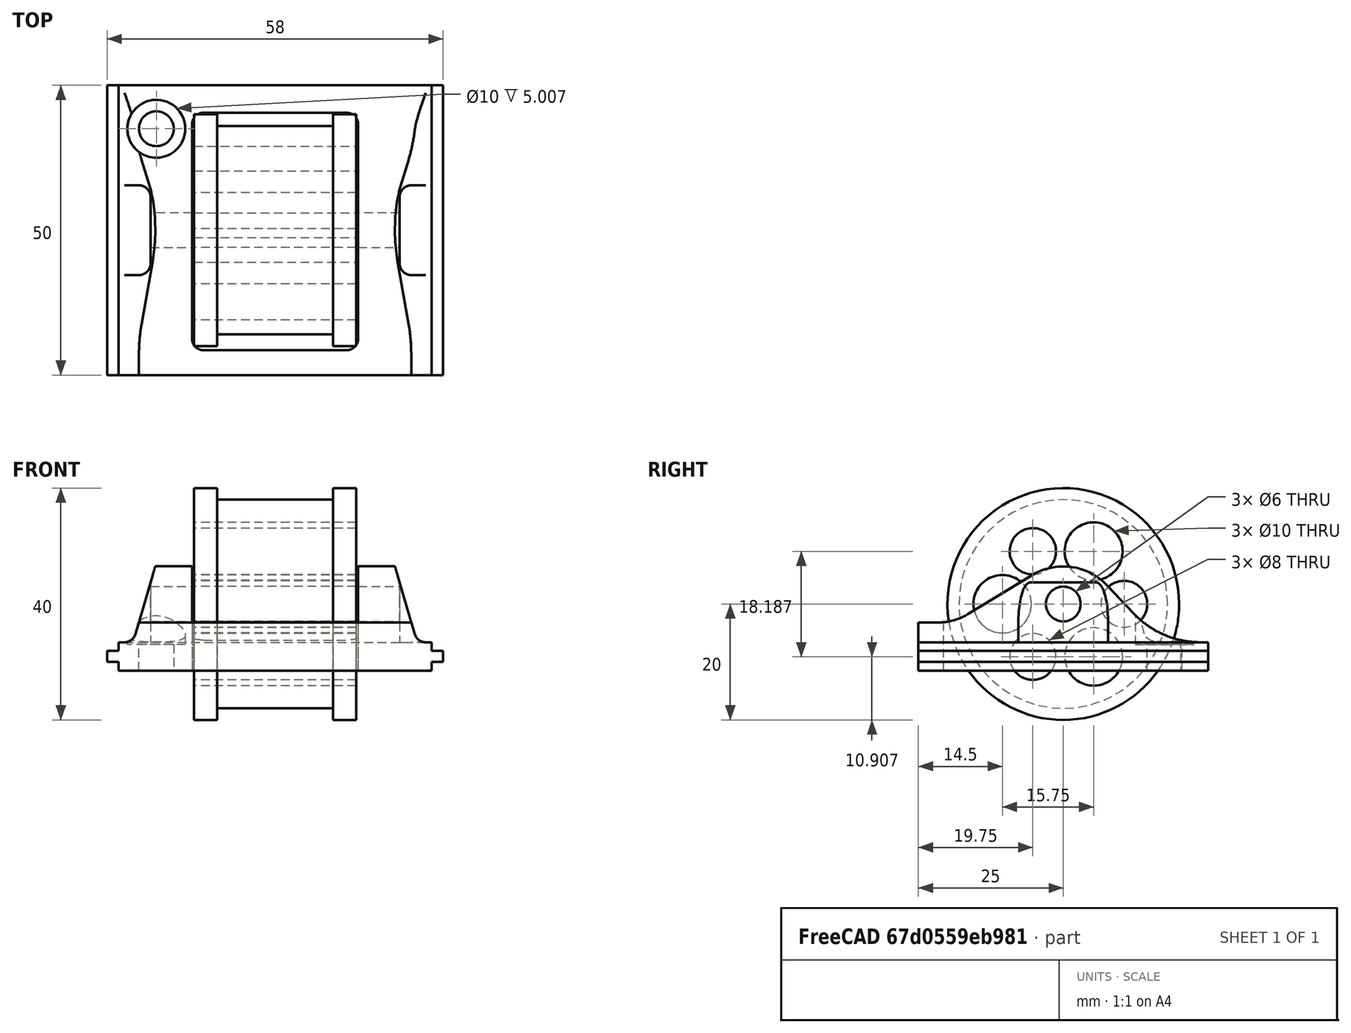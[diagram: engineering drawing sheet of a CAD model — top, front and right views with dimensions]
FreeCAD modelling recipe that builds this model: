
FCSTD DOCUMENT  (FreeCAD 0.22R35966 (Git))
Label: pusher
License: All rights reserved
LicenseURL: http://en.wikipedia.org/wiki/All_rights_reserved
objects: Sketcher::SketchObject×9, TechDraw::DrawViewDimension×9, PartDesign::Pocket×6, TechDraw::DrawProjGroupItem×3, PartDesign::Pad×2, PartDesign::Plane×2, PartDesign::Body×2, App::Part×2, Spreadsheet::Sheet×1, TechDraw::DrawProjGroup×1, TechDraw::DrawViewPart×1, TechDraw::DrawViewAnnotation×1, TechDraw::DrawViewSection×1, TechDraw::DrawViewSymbol×1, TechDraw::DrawSVGTemplate×1, TechDraw::DrawPage×1
note: 29 computed .brp shape members not serialized (recipe doc carries the construction recipe); baked Part::Feature solids carry a one-line shape summary decoded from their .brp

FEATURE [Spreadsheet::Sheet] Spreadsheet  label="dim"
  cells = A2='Rail Height; B2(railHeight)=2; A3='Spring OD; B3(springOD)=40; A4='Rail from floor; B4(railFromFloor)=10; A5='Spring ID; B5(springID)=36; A6='spring Width; B6(springWidth)=20; A7='cylinder Width; B7(cylinderWidth)==springWidth + 8; A8='Rail Width; B8(railWidth)=58; A9='Rail top; B9(railTop)=1.5; A10='Axis OD; B10(axisOD)=6; A11='pilar Width; B11(pilarWidth)=6; A12='Rail Depth; B12(RailDepth)=2; A13='RBF OD; B13(RBFOD)=6; A14='RBF Seating D; B14(RBFSeatingD)=10; A15='RBF From Sat; B15(RBFFromSat)=7.5; A16='RBF From Rail; B16(RBFFromRail)=6.5
FEATURE [Sketcher::SketchObject] Sketch001
  FullyConstrained = false
  MapMode = 5
  Placement = pos=(0,0,0) rot=(0.57735,0.57735,0.57735;2.0944rad)
  Support = -> [YZ_Plane]
  expr: Constraints[10] = Sketch.Constraints[10]
  expr: Constraints[11] = Sketch.Constraints[11]
  expr: Constraints[12] = Sketch.Constraints[12]
  expr: Constraints[13] = Sketch.Constraints[13]
  expr: Constraints[16] = Sketch.Constraints[16]
  expr: Constraints[9] = Sketch.Constraints[9]
  sketch-geometry (21):
    g0: LineSegment StartX=-43.3303 StartY=12 StartZ=0 EndX=0 EndY=12 EndZ=0
    g1: LineSegment StartX=0 StartY=12 StartZ=0 EndX=0 EndY=10 EndZ=0
    g2: LineSegment StartX=0 StartY=10 StartZ=0 EndX=-43.3303 EndY=10 EndZ=0
    g3: LineSegment StartX=-43.3303 StartY=10 StartZ=0 EndX=-43.3303 EndY=12 EndZ=0
    g4: Circle CenterX=-25 CenterY=20 CenterZ=0 NormalX=0 NormalY=0 NormalZ=1 AngleXU=0 Radius=20
    g5: Circle CenterX=-25 CenterY=20 CenterZ=0 NormalX=0 NormalY=0 NormalZ=1 AngleXU=0 Radius=18
    g6: Circle CenterX=-25 CenterY=20 CenterZ=0 NormalX=0 NormalY=0 NormalZ=1 AngleXU=0 Radius=20
    g7: Circle CenterX=-25 CenterY=20 CenterZ=0 NormalX=0 NormalY=0 NormalZ=1 AngleXU=0 Radius=3
    g8: LineSegment StartX=-19.75 StartY=29.0933 StartZ=0 EndX=-30.25 EndY=29.0933 EndZ=0
    g9: LineSegment StartX=-30.25 StartY=29.0933 StartZ=0 EndX=-35.5 EndY=20 EndZ=0
    g10: LineSegment StartX=-35.5 StartY=20 StartZ=0 EndX=-30.25 EndY=10.9067 EndZ=0
    g11: LineSegment StartX=-30.25 StartY=10.9067 StartZ=0 EndX=-19.75 EndY=10.9067 EndZ=0
    g12: LineSegment StartX=-19.75 StartY=10.9067 StartZ=0 EndX=-14.5 EndY=20 EndZ=0
    g13: LineSegment StartX=-14.5 StartY=20 StartZ=0 EndX=-19.75 EndY=29.0933 EndZ=0
    g14: Circle CenterX=-25 CenterY=20 CenterZ=0 NormalX=0 NormalY=0 NormalZ=1 AngleXU=0 Radius=10.5
    g15: Circle CenterX=-19.75 CenterY=29.0933 CenterZ=0 NormalX=0 NormalY=0 NormalZ=1 AngleXU=0 Radius=5
    g16: Circle CenterX=-14.5 CenterY=20 CenterZ=0 NormalX=0 NormalY=0 NormalZ=1 AngleXU=0 Radius=4
    g17: Circle CenterX=-19.75 CenterY=10.9067 CenterZ=0 NormalX=0 NormalY=0 NormalZ=1 AngleXU=0 Radius=5
    g18: Circle CenterX=-30.25 CenterY=10.9067 CenterZ=0 NormalX=0 NormalY=0 NormalZ=1 AngleXU=0 Radius=4
    g19: Circle CenterX=-35.5 CenterY=20 CenterZ=0 NormalX=0 NormalY=0 NormalZ=1 AngleXU=0 Radius=5
    g20: Circle CenterX=-30.25 CenterY=29.0933 CenterZ=0 NormalX=0 NormalY=0 NormalZ=1 AngleXU=0 Radius=4
  constraints (49):
    c: Coincident(g0,g1)
    c: Coincident(g1,g2)
    c: Coincident(g2,g3)
    c: Coincident(g3,g0)
    c: Horizontal(g0)
    c: Horizontal(g2)
    c: Vertical(g1)
    c: Vertical(g3)
    c: PointOnObject(g0,g-2)
    c: Diameter(g4) = 40
    c: DistanceY(g-1,g4) = 20
    c: DistanceX(g4,g-1) = 25
    c: DistanceY(g1,g1) = 2
    c: DistanceY(g-1,g1) = 10
    c: PointOnObject(g0,g4)
    c: Coincident(g5,g4)
    c: Diameter(g5) = 36
    c: Coincident(g6,g4)
    c: Equal(g6,g4)
    c: Coincident(g7,g6)
    c: Diameter(g7) = 6
    c: Coincident(g8,g9)
    c: Coincident(g9,g10)
    c: Coincident(g10,g11)
    c: Coincident(g11,g12)
    c: Coincident(g12,g13)
    c: Coincident(g13,g8)
    c: Equal(g8, g9-g13) x5
    c: PointOnObject(g8,g14)
    c: PointOnObject(g9,g14)
    c: PointOnObject(g10,g14)
    c: PointOnObject(g11,g14)
    c: PointOnObject(g12,g14)
    c: PointOnObject(g13,g14)
    c: Horizontal(g8)
    c: Coincident(g14,g6)
    c: Coincident(g15,g8)
    c: Coincident(g16,g12)
    c: Coincident(g17,g11)
    c: Coincident(g18,g10)
    c: Coincident(g19,g9)
    c: Coincident(g20,g8)
    c: Diameter(g20) = 8
    c: Equal(g20,g16)
    c: Equal(g20,g18)
    c: Diameter(g15) = 10
    c: Equal(g15,g17)
    c: Equal(g15,g19)
    c: Diameter(g14) = 21
FEATURE [PartDesign::Pad] Pad
  AllowMultiFace = false
  Direction = (1,1,1)
  Length = 28
  Length2 = 100
  Midplane = true
  Placement = pos=(0,0,0) rot=(0.57735,0.57735,0.57735;2.0944rad)
  Profile = -> Sketch001
  Suppressed = false
  Type = 0
  expr: Length = <<dim>>.cylinderWidth
FEATURE [Sketcher::SketchObject] Sketch002
  FullyConstrained = false
  MapMode = 5
  Placement = pos=(0,0,0) rot=(0.57735,0.57735,0.57735;2.0944rad)
  Support = -> [YZ_Plane]
  expr: Constraints[10] = Sketch.Constraints[10]
  expr: Constraints[11] = Sketch.Constraints[11]
  expr: Constraints[12] = Sketch.Constraints[12]
  expr: Constraints[13] = Sketch.Constraints[13]
  expr: Constraints[16] = Sketch.Constraints[16]
  expr: Constraints[9] = Sketch.Constraints[9]
  sketch-geometry (6):
    g0: LineSegment StartX=-43.3303 StartY=12 StartZ=0 EndX=0 EndY=12 EndZ=0
    g1: LineSegment StartX=0 StartY=12 StartZ=0 EndX=0 EndY=10 EndZ=0
    g2: LineSegment StartX=0 StartY=10 StartZ=0 EndX=-43.3303 EndY=10 EndZ=0
    g3: LineSegment StartX=-43.3303 StartY=10 StartZ=0 EndX=-43.3303 EndY=12 EndZ=0
    g4: Circle CenterX=-25 CenterY=20 CenterZ=0 NormalX=0 NormalY=0 NormalZ=1 AngleXU=0 Radius=20
    g5: Circle CenterX=-25 CenterY=20 CenterZ=0 NormalX=0 NormalY=0 NormalZ=1 AngleXU=0 Radius=18
  constraints (17):
    c: Coincident(g0,g1)
    c: Coincident(g1,g2)
    c: Coincident(g2,g3)
    c: Coincident(g3,g0)
    c: Horizontal(g0)
    c: Horizontal(g2)
    c: Vertical(g1)
    c: Vertical(g3)
    c: PointOnObject(g0,g-2)
    c: Diameter(g4) = 40
    c: DistanceY(g-1,g4) = 20
    c: DistanceX(g4,g-1) = 25
    c: DistanceY(g1,g1) = 2
    c: DistanceY(g-1,g1) = 10
    c: PointOnObject(g0,g4)
    c: Coincident(g5,g4)
    c: Diameter(g5) = 36
FEATURE [PartDesign::Pocket] Pocket
  AllowMultiFace = false
  BaseFeature = -> Pad
  Direction = (1,1,1)
  Length = 20
  Length2 = 100
  Midplane = true
  Placement = pos=(0,0,0) rot=(0.57735,0.57735,0.57735;2.0944rad)
  Profile = -> Sketch002
  Suppressed = false
  Type = 0
  expr: Length = <<dim>>.springWidth
FEATURE [Sketcher::SketchObject] Sketch003
  FullyConstrained = false
  MapMode = 5
  Placement = pos=(0,0,0) rot=(1,0,0;1.5708rad)
  Support = -> [XZ_Plane001]
  expr: Constraints[31] = <<dim>>.railFromFloor
  expr: Constraints[37] = <<dim>>.railHeight - 0.1
  expr: Constraints[44] = <<dim>>.railWidth
  expr: Constraints[45] = <<dim>>.RailDepth
  sketch-geometry (20):
    g0: LineSegment StartX=27 StartY=8.5 StartZ=0 EndX=27 EndY=10 EndZ=0
    g1: LineSegment StartX=27 StartY=10 StartZ=0 EndX=29 EndY=10 EndZ=0
    g2: LineSegment StartX=29 StartY=10 StartZ=0 EndX=29 EndY=11.9 EndZ=0
    g3: LineSegment StartX=29 StartY=11.9 StartZ=0 EndX=27 EndY=11.9 EndZ=0
    g4: LineSegment StartX=27 StartY=11.9 StartZ=0 EndX=27 EndY=13.4 EndZ=0
    g5: LineSegment StartX=27 StartY=13.4 StartZ=0 EndX=26 EndY=13.4 EndZ=0
    g6: LineSegment StartX=24.0797 StartY=14.8411 StartZ=0 EndX=20.25 EndY=28 EndZ=0
    g7: LineSegment StartX=20.25 StartY=28 StartZ=0 EndX=14.25 EndY=28 EndZ=0
    g8: LineSegment StartX=-27 StartY=8.5 StartZ=0 EndX=-27 EndY=10 EndZ=0
    g9: LineSegment StartX=-27 StartY=10 StartZ=0 EndX=-29 EndY=10 EndZ=0
    g10: LineSegment StartX=-29 StartY=10 StartZ=0 EndX=-29 EndY=11.9 EndZ=0
    g11: LineSegment StartX=-29 StartY=11.9 StartZ=0 EndX=-27 EndY=11.9 EndZ=0
    g12: LineSegment StartX=-27 StartY=11.9 StartZ=0 EndX=-27 EndY=13.4 EndZ=0
    g13: LineSegment StartX=-27 StartY=13.4 StartZ=0 EndX=-26 EndY=13.4 EndZ=0
    g14: LineSegment StartX=-24.0797 StartY=14.8411 StartZ=0 EndX=-20.25 EndY=28 EndZ=0
    g15: LineSegment StartX=-20.25 StartY=28 StartZ=0 EndX=-14.25 EndY=28 EndZ=0
    g16: LineSegment StartX=14.25 StartY=28 StartZ=0 EndX=-14.25 EndY=28 EndZ=0
    g17: LineSegment StartX=-27 StartY=8.5 StartZ=0 EndX=27 EndY=8.5 EndZ=0
    g18: ArcOfCircle CenterX=-26 CenterY=15.4 CenterZ=0 NormalX=0 NormalY=0 NormalZ=1 AngleXU=0 Radius=2 StartAngle=4.71239 EndAngle=5.99997
    g19: ArcOfCircle CenterX=26 CenterY=15.4 CenterZ=0 NormalX=0 NormalY=0 NormalZ=1 AngleXU=0 Radius=2 StartAngle=3.4248 EndAngle=4.71239
  constraints (57):
    c: Vertical(g0)
    c: Coincident(g0,g1)
    c: Horizontal(g1)
    c: Coincident(g1,g2)
    c: Vertical(g2)
    c: Coincident(g2,g3)
    c: Horizontal(g3)
    c: Coincident(g3,g4)
    c: Coincident(g4,g5)
    c: Horizontal(g5)
    c: Coincident(g6,g7)
    c: Horizontal(g7)
    c: Vertical(g4)
    c: PointOnObject(g3,g0)
    c: Vertical(g8)
    c: Coincident(g8,g9)
    c: Horizontal(g9)
    c: Coincident(g9,g10)
    c: Vertical(g10)
    c: Coincident(g10,g11)
    c: Horizontal(g11)
    c: Coincident(g11,g12)
    c: Coincident(g12,g13)
    c: Horizontal(g13)
    c: Coincident(g14,g15)
    c: Horizontal(g15)
    c: Vertical(g12)
    c: PointOnObject(g11,g8)
    c: Coincident(g17,g8)
    c: Coincident(g17,g0)
    c: Symmetric(g8,g0,g-2)
    c: DistanceY(g-1,g9) = 10
    c: Equal(g8,g0)
    c: Equal(g9,g1)
    c: Equal(g2,g10)
    c: Equal(g12,g4)
    c: Equal(g5,g13)
    c: DistanceY(g10,g10) = 1.9
    c: Equal(g8,g12)
    c: DistanceY(g12,g12) = 1.5
    c: Equal(g15,g7)
    c: DistanceX(g16,g16) = 28.5
    c: DistanceY(g-1,g15) = 28  'pilarHeight'
    c: DistanceX(g15,g15) = 6
    c: DistanceX(g9,g1) = 58
    c: DistanceX(g1,g1) = 2
    c: Tangent(g14,g18) = -1.5708
    c: Tangent(g13,g18) = -1.5708
    c: Tangent(g6,g19) = 1.5708
    c: Tangent(g5,g19) = 1.5708
    c: Equal(g18,g19)
    c: Equal(g13,g5)
    c: Radius(g18) = 2
    c: DistanceX(g12,g18) = 1
    c: Coincident(g16,g15)
    c: Coincident(g16,g7)
    c: Symmetric(g7,g15,g-2)
FEATURE [PartDesign::Pad] Pad001
  AllowMultiFace = false
  Direction = (1,1,1)
  Length = 50
  Length2 = 100
  Placement = pos=(0,0,0) rot=(1,0,0;1.5708rad)
  Profile = -> Sketch003
  Suppressed = false
  Type = 0
FEATURE [Sketcher::SketchObject] Sketch004  label="baseSketch001"
  FullyConstrained = false
  MapMode = 5
  Placement = pos=(0,0,0) rot=(0.57735,0.57735,0.57735;2.0944rad)
  Support = -> [YZ_Plane001]
  expr: Constraints[18] = <<dim>>.axisOD
  expr: Constraints[36] = 10 + 1.9 + 1.5
  expr: Constraints[9] = <<dim>>.springOD
  sketch-geometry (19):
    g0: LineSegment StartX=-43.3303 StartY=12 StartZ=0 EndX=0 EndY=12 EndZ=0
    g1: LineSegment StartX=0 StartY=12 StartZ=0 EndX=0 EndY=10 EndZ=0
    g2: LineSegment StartX=0 StartY=10 StartZ=0 EndX=-43.3303 EndY=10 EndZ=0
    g3: LineSegment StartX=-43.3303 StartY=10 StartZ=0 EndX=-43.3303 EndY=12 EndZ=0
    g4: Circle CenterX=-25 CenterY=20 CenterZ=0 NormalX=0 NormalY=0 NormalZ=1 AngleXU=0 Radius=20
    g5: Circle CenterX=-25 CenterY=20 CenterZ=0 NormalX=0 NormalY=0 NormalZ=1 AngleXU=0 Radius=18
    g6: Circle CenterX=-25 CenterY=20 CenterZ=0 NormalX=0 NormalY=0 NormalZ=1 AngleXU=0 Radius=3
    g7: LineSegment StartX=-41.4553 StartY=18.2442 StartZ=0 EndX=-30.3662 EndY=24.9932 EndZ=0
    g8: LineSegment StartX=-17.5118 StartY=23.2798 StartZ=0 EndX=-12.821 EndY=18.3352 EndZ=0
    g9: LineSegment StartX=-1.33651 StartY=13.4 StartZ=0 EndX=5.50918 EndY=13.4 EndZ=0
    g10: LineSegment StartX=5.50918 StartY=13.4 StartZ=0 EndX=5.50918 EndY=39.591 EndZ=0
    g11: LineSegment StartX=5.50918 StartY=39.591 StartZ=0 EndX=-54.9003 EndY=39.591 EndZ=0
    g12: LineSegment StartX=-54.9003 StartY=39.591 StartZ=0 EndX=-54.9003 EndY=16.8241 EndZ=0
    g13: LineSegment StartX=-25 StartY=47.8975 StartZ=0 EndX=-25 EndY=-22.7529 EndZ=0
    g14: ArcOfCircle CenterX=-1.33651 CenterY=29.2301 CenterZ=0 NormalX=0 NormalY=0 NormalZ=1 AngleXU=0 Radius=15.8301 StartAngle=3.90065 EndAngle=4.71239
    g15: ArcOfCircle CenterX=-25 CenterY=16.176 CenterZ=0 NormalX=0 NormalY=0 NormalZ=1 AngleXU=0 Radius=10.3217 StartAngle=0.759059 EndAngle=2.11752
    g16: GeomPoint X=-25 Y=26.4977 Z=0
    g17: LineSegment StartX=-54.9003 StartY=16.8241 StartZ=0 EndX=-46.5205 EndY=16.8241 EndZ=0
    g18: ArcOfCircle CenterX=-46.5205 CenterY=26.5668 CenterZ=0 NormalX=0 NormalY=0 NormalZ=1 AngleXU=0 Radius=9.74273 StartAngle=4.71239 EndAngle=5.25911
  constraints (43):
    c: Coincident(g0,g1)
    c: Coincident(g1,g2)
    c: Coincident(g2,g3)
    c: Coincident(g3,g0)
    c: Horizontal(g0)
    c: Horizontal(g2)
    c: Vertical(g1)
    c: Vertical(g3)
    c: PointOnObject(g0,g-2)
    c: Diameter(g4) = 40
    c: DistanceY(g-1,g4) = 20  'H'
    c: DistanceX(g4,g-1) = 25  'centerFromBack'
    c: DistanceY(g1,g1) = 2
    c: DistanceY(g-1,g1) = 10
    c: PointOnObject(g0,g4)
    c: Coincident(g5,g4)
    c: Diameter(g5) = 36
    c: Coincident(g6,g4)
    c: Diameter(g6) = 6
    c: Horizontal(g9)
    c: Coincident(g9,g10)
    c: Vertical(g10)
    c: Coincident(g10,g11)
    c: Horizontal(g11)
    c: Coincident(g11,g12)
    c: Vertical(g12)
    c: PointOnObject(g6,g13)
    c: Tangent(g8,g14) = -1.5708
    c: Tangent(g9,g14) = -1.5708
    c: PointOnObject(g15,g13)
    c: Coincident(g15,g7)
    c: Coincident(g15,g8)
    c: Tangent(g7,g15) = 1.5708
    c: Tangent(g8,g15) = 1.5708
    c: PointOnObject(g16,g15)
    c: PointOnObject(g16,g13)
    c: DistanceY(g-1,g9) = 13.4
    c: Vertical(g13)
    c: Coincident(g17,g12)
    c: Coincident(g18,g7)
    c: Tangent(g7,g18) = -1.5708
    c: Horizontal(g17)
    c: Tangent(g17,g18) = -1.5708
FEATURE [PartDesign::Pocket] Pocket001
  AllowMultiFace = false
  BaseFeature = -> Pad001
  Direction = (1,1,1)
  Length = 5
  Length2 = 100
  Midplane = true
  Placement = pos=(0,0,0) rot=(1,0,0;1.5708rad)
  Profile = -> Sketch004
  Suppressed = false
  Type = 1
FEATURE [PartDesign::Plane] DatumPlane
  AttachmentOffset = pos=(0,0,28) rot=(0,0,1;0rad)
  Length = 71.1909
  MapMode = 3
  Placement = pos=(0,0,28) rot=(0,0,1;3.14159rad)
  ResizeMode = 0
  Support = -> [Pocket001]
  Width = 88.1909
FEATURE [Sketcher::SketchObject] Sketch005
  FullyConstrained = false
  MapMode = 5
  Placement = pos=(0,0,28) rot=(0,0,1;3.14159rad)
  Support = -> [DatumPlane]
  expr: Constraints[31] = <<dim>>.railWidth
  expr: Constraints[6] = Sketch004.Constraints.centerFromBack
  sketch-geometry (13):
    g0: LineSegment StartX=-29 StartY=32.75 StartZ=0 EndX=-23.5 EndY=32.75 EndZ=0
    g1: LineSegment StartX=-21.5 StartY=30.75 StartZ=0 EndX=-21.5 EndY=19.25 EndZ=0
    g2: LineSegment StartX=-23.5 StartY=17.25 StartZ=0 EndX=-29 EndY=17.25 EndZ=0
    g3: LineSegment StartX=-29 StartY=17.25 StartZ=0 EndX=-29 EndY=32.75 EndZ=0
    g4: LineSegment StartX=-29 StartY=25 StartZ=0 EndX=29 EndY=25 EndZ=0
    g5: ArcOfCircle CenterX=-23.5 CenterY=30.75 CenterZ=0 NormalX=0 NormalY=0 NormalZ=1 AngleXU=0 Radius=2 StartAngle=5e-16 EndAngle=1.5708
    g6: ArcOfCircle CenterX=-23.5 CenterY=19.25 CenterZ=0 NormalX=0 NormalY=0 NormalZ=1 AngleXU=0 Radius=2 StartAngle=4.71239 EndAngle=6.28319
    g7: LineSegment StartX=29 StartY=32.75 StartZ=0 EndX=23.5 EndY=32.75 EndZ=0
    g8: LineSegment StartX=21.5 StartY=30.75 StartZ=0 EndX=21.5 EndY=19.25 EndZ=0
    g9: LineSegment StartX=23.5 StartY=17.25 StartZ=0 EndX=29 EndY=17.25 EndZ=0
    g10: LineSegment StartX=29 StartY=17.25 StartZ=0 EndX=29 EndY=32.75 EndZ=0
    g11: ArcOfCircle CenterX=23.5 CenterY=30.75 CenterZ=0 NormalX=0 NormalY=0 NormalZ=1 AngleXU=0 Radius=2 StartAngle=1.5708 EndAngle=3.14159
    g12: ArcOfCircle CenterX=23.5 CenterY=19.25 CenterZ=0 NormalX=0 NormalY=0 NormalZ=1 AngleXU=0 Radius=2 StartAngle=3.14159 EndAngle=4.71239
  constraints (32):
    c: Coincident(g2,g3)
    c: Coincident(g3,g0)
    c: Horizontal(g0)
    c: Horizontal(g2)
    c: Vertical(g3)
    c: Horizontal(g4)
    c: DistanceY(g-1,g4) = 25
    c: Tangent(g1,g5) = 1.5708
    c: Tangent(g0,g5) = 1.5708
    c: Tangent(g1,g6) = 1.5708
    c: Tangent(g2,g6) = 1.5708
    c: Equal(g6,g5)
    c: Radius(g5) = 2
    c: Symmetric(g1,g1,g4)
    c: DistanceY(g1,g1) = 11.5
    c: Coincident(g9,g10)
    c: Coincident(g10,g7)
    c: Horizontal(g7)
    c: Horizontal(g9)
    c: Vertical(g10)
    c: Tangent(g8,g11) = -1.5708
    c: Tangent(g7,g11) = -1.5708
    c: Tangent(g8,g12) = -1.5708
    c: Tangent(g9,g12) = -1.5708
    c: Equal(g12,g11)
    c: Symmetric(g8,g1,g-2)
    c: DistanceX(g1,g8) = 43
    c: Symmetric(g8,g8,g4)
    c: PointOnObject(g4,g3)
    c: PointOnObject(g4,g10)
    c: Symmetric(g9,g2,g-2)
    c: DistanceX(g0,g7) = 58
FEATURE [PartDesign::Pocket] Pocket002
  AllowMultiFace = false
  BaseFeature = -> Pocket001
  Direction = (1,1,1)
  Length = 14.6
  Length2 = 100
  Placement = pos=(0,0,0) rot=(1,0,0;1.5708rad)
  Profile = -> Sketch005
  Suppressed = false
  Type = 0
FEATURE [Sketcher::SketchObject] Sketch006
  FullyConstrained = false
  MapMode = 5
  Support = -> [XY_Plane001]
  sketch-geometry (8):
    g0: LineSegment StartX=-12.3486 StartY=-4.73756 StartZ=0 EndX=12.3447 EndY=-4.73756 EndZ=0
    g1: LineSegment StartX=14.3447 StartY=-6.73756 StartZ=0 EndX=14.3447 EndY=-43.7105 EndZ=0
    g2: LineSegment StartX=12.3447 StartY=-45.7105 StartZ=0 EndX=-12.3486 EndY=-45.7105 EndZ=0
    g3: LineSegment StartX=-14.3486 StartY=-43.7105 StartZ=0 EndX=-14.3486 EndY=-6.73756 EndZ=0
    g4: ArcOfCircle CenterX=12.3447 CenterY=-6.73756 CenterZ=0 NormalX=0 NormalY=0 NormalZ=1 AngleXU=0 Radius=2 StartAngle=1e-16 EndAngle=1.5708
    g5: ArcOfCircle CenterX=-12.3486 CenterY=-6.73756 CenterZ=0 NormalX=0 NormalY=0 NormalZ=1 AngleXU=0 Radius=2 StartAngle=1.5708 EndAngle=3.14159
    g6: ArcOfCircle CenterX=-12.3486 CenterY=-43.7105 CenterZ=0 NormalX=0 NormalY=0 NormalZ=1 AngleXU=0 Radius=2 StartAngle=3.14159 EndAngle=4.71239
    g7: ArcOfCircle CenterX=12.3447 CenterY=-43.7105 CenterZ=0 NormalX=0 NormalY=0 NormalZ=1 AngleXU=0 Radius=2 StartAngle=4.71239 EndAngle=6.28319
  constraints (16):
    c: Horizontal(g0)
    c: Horizontal(g2)
    c: Vertical(g1)
    c: Vertical(g3)
    c: Tangent(g1,g4) = 1.5708
    c: Tangent(g0,g4) = 1.5708
    c: Tangent(g0,g5) = 1.5708
    c: Tangent(g3,g5) = 1.5708
    c: Tangent(g3,g6) = 1.5708
    c: Tangent(g2,g6) = 1.5708
    c: Tangent(g1,g7) = 1.5708
    c: Tangent(g2,g7) = 1.5708
    c: Equal(g4,g5)
    c: Equal(g5,g6)
    c: Equal(g6,g7)
    c: Radius(g4) = 2
FEATURE [PartDesign::Pocket] Pocket003
  AllowMultiFace = false
  BaseFeature = -> Pocket002
  Direction = (1,1,1)
  Length = 5
  Length2 = 100
  Midplane = true
  Placement = pos=(0,0,0) rot=(1,0,0;1.5708rad)
  Profile = -> Sketch006
  Reversed = true
  Suppressed = false
  Type = 1
FEATURE [PartDesign::Plane] DatumPlane001
  AttachmentOffset = pos=(0,0,18) rot=(0,0,1;0rad)
  Length = 71.1909
  MapMode = 5
  Placement = pos=(0,0,18) rot=(0,0,1;0rad)
  ResizeMode = 0
  Support = -> [XY_Plane001]
  Width = 88.1909
FEATURE [Sketcher::SketchObject] Sketch007
  FullyConstrained = false
  MapMode = 5
  Placement = pos=(0,0,18) rot=(0,0,1;0rad)
  Support = -> [DatumPlane001]
  expr: Constraints[0] = <<dim>>.RBFSeatingD
  expr: Constraints[1] = <<dim>>.RBFFromSat
  expr: Constraints[2] = <<dim>>.railWidth / 2 - <<dim>>.RailDepth - <<dim>>.RBFFromRail
  sketch-geometry (1):
    g0: Circle CenterX=-20.5 CenterY=-7.5 CenterZ=0 NormalX=0 NormalY=0 NormalZ=1 AngleXU=0 Radius=5
  constraints (3):
    c: Diameter(g0) = 10
    c: DistanceY(g0,g-1) = 7.5
    c: DistanceX(g0,g-1) = 20.5
FEATURE [PartDesign::Pocket] Pocket004
  AllowMultiFace = false
  BaseFeature = -> Pocket003
  Direction = (1,1,1)
  Length = 10
  Length2 = 100
  Midplane = true
  Placement = pos=(0,0,0) rot=(1,0,0;1.5708rad)
  Profile = -> Sketch007
  Suppressed = false
  Type = 0
FEATURE [Sketcher::SketchObject] Sketch008
  FullyConstrained = false
  MapMode = 5
  Placement = pos=(0,0,18) rot=(0,0,1;0rad)
  Support = -> [DatumPlane001]
  expr: Constraints[0] = <<dim>>.RBFOD
  expr: Constraints[1] = <<dim>>.RBFFromSat
  expr: Constraints[2] = <<dim>>.railWidth / 2 - <<dim>>.RailDepth - <<dim>>.RBFFromRail
  sketch-geometry (1):
    g0: Circle CenterX=-20.5 CenterY=-7.5 CenterZ=0 NormalX=0 NormalY=0 NormalZ=1 AngleXU=0 Radius=3
  constraints (3):
    c: Diameter(g0) = 6
    c: DistanceY(g0,g-1) = 7.5
    c: DistanceX(g0,g-1) = 20.5
FEATURE [PartDesign::Pocket] Pocket005
  AllowMultiFace = false
  BaseFeature = -> Pocket004
  Direction = (1,1,1)
  Length = 5
  Length2 = 100
  Placement = pos=(0,0,0) rot=(1,0,0;1.5708rad)
  Profile = -> Sketch008
  Suppressed = false
  Type = 1
FEATURE [Sketcher::SketchObject] Sketch  label="baseSketch"
  FullyConstrained = true
  MapMode = 5
  Placement = pos=(-21.5,0,0) rot=(0.707107,0,-0.707107;3.14159rad)
  Support = -> [Pocket005]
  expr: Constraints[10] = <<dim>>.springOD / 2
  expr: Constraints[11] = <<dim>>.springOD / 2 + 5
  expr: Constraints[12] = <<dim>>.railHeight
  expr: Constraints[13] = <<dim>>.railFromFloor
  expr: Constraints[16] = <<dim>>.springID
  expr: Constraints[9] = <<dim>>.springOD
  sketch-geometry (6):
    g0: LineSegment StartX=-43.3303 StartY=12 StartZ=0 EndX=0 EndY=12 EndZ=0
    g1: LineSegment StartX=0 StartY=12 StartZ=0 EndX=0 EndY=10 EndZ=0
    g2: LineSegment StartX=0 StartY=10 StartZ=0 EndX=-43.3303 EndY=10 EndZ=0
    g3: LineSegment StartX=-43.3303 StartY=10 StartZ=0 EndX=-43.3303 EndY=12 EndZ=0
    g4: Circle CenterX=-25 CenterY=20 CenterZ=0 NormalX=0 NormalY=0 NormalZ=1 AngleXU=0 Radius=20
    g5: Circle CenterX=-25 CenterY=20 CenterZ=0 NormalX=0 NormalY=0 NormalZ=1 AngleXU=0 Radius=18
  constraints (17):
    c: Coincident(g0,g1)
    c: Coincident(g1,g2)
    c: Coincident(g2,g3)
    c: Coincident(g3,g0)
    c: Horizontal(g0)
    c: Horizontal(g2)
    c: Vertical(g1)
    c: Vertical(g3)
    c: PointOnObject(g0,g-2)
    c: Diameter(g4) = 40
    c: DistanceY(g-1,g4) = 20
    c: DistanceX(g4,g-1) = 25
    c: DistanceY(g1,g1) = 2
    c: DistanceY(g-1,g1) = 10
    c: PointOnObject(g0,g4)
    c: Coincident(g5,g4)
    c: Diameter(g5) = 36
FEATURE [PartDesign::Body] Body  label="SpoolBody"
  Group = -> [Sketch,Sketch001,Pad,Sketch002,Pocket]
  Origin = -> Origin
  Tip = -> Pocket
FEATURE [PartDesign::Body] Body001  label="PusherBody"
  Group = -> [Sketch003,Pad001,Sketch004,Pocket001,DatumPlane,Sketch005,Pocket002,Sketch006,Pocket003,DatumPlane001,Sketch007,Pocket004,Sketch008,Pocket005]
  Origin = -> Origin001
  Tip = -> Pocket005
FEATURE [TechDraw::DrawProjGroupItem] ProjItem  label="Front"
  CoarseView = false
  Direction = (0,1,0)
  Focus = 100
  HardHidden = false
  IsoCount = 0
  IsoHidden = false
  IsoVisible = false
  LockPosition = true
  Perspective = false
  Rotation = 0
  RotationVector = (-1,0,2e-16)
  ScaleType = 2
  ScrubCount = 0
  SeamHidden = false
  SeamVisible = false
  SmoothHidden = false
  SmoothVisible = false
  Source = -> [Body001]
  Type = 0
  X = 0
  XDirection = (-1,0,2e-16)
  Y = 0
FEATURE [TechDraw::DrawViewDimension] Dimension
  AngleOverride = false
  Arbitrary = false
  ArbitraryTolerances = false
  EqualTolerance = false
  ExtensionAngle = 0
  FormatSpec = %.2f
  FormatSpecOverTolerance = %+.2w
  FormatSpecUnderTolerance = %+.2w
  Inverted = false
  LineAngle = 0
  LockPosition = false
  MeasureType = 1
  OverTolerance = 0
  References2D = -> [ProjItem]
  Rotation = 0
  ScaleType = 0
  TheoreticalExact = false
  Type = 2
  UnderTolerance = -0.1
  X = 36.6294
  Y = 6.67132
FEATURE [TechDraw::DrawViewDimension] Dimension002
  AngleOverride = false
  Arbitrary = false
  ArbitraryTolerances = false
  EqualTolerance = false
  ExtensionAngle = 0
  FormatSpec = %.2f
  FormatSpecOverTolerance = %+.2w
  FormatSpecUnderTolerance = %+.2w
  Inverted = false
  LineAngle = 0
  LockPosition = false
  MeasureType = 1
  OverTolerance = 0.2
  References2D = -> [ProjItem]
  Rotation = 0
  ScaleType = 0
  TheoreticalExact = false
  Type = 1
  UnderTolerance = 0
  X = -2.72566
  Y = -27.6367
FEATURE [TechDraw::DrawViewDimension] Dimension001
  AngleOverride = false
  Arbitrary = false
  ArbitraryTolerances = false
  EqualTolerance = false
  ExtensionAngle = 0
  FormatSpec = %.2f
  FormatSpecOverTolerance = %+.2w
  FormatSpecUnderTolerance = %+.2w
  Inverted = false
  LineAngle = 0
  LockPosition = false
  MeasureType = 1
  OverTolerance = 0
  References2D = -> [ProjItem]
  Rotation = 0
  ScaleType = 0
  TheoreticalExact = false
  Type = 1
  UnderTolerance = -0.1
  X = -1.94598
  Y = -18.3684
FEATURE [TechDraw::DrawProjGroupItem] ProjItem001  label="Top"
  CoarseView = false
  Direction = (2e-16,0,1)
  Focus = 100
  HardHidden = false
  IsoCount = 0
  IsoHidden = false
  IsoVisible = false
  LockPosition = false
  Perspective = false
  Rotation = 0
  RotationVector = (-1,0,2e-16)
  ScaleType = 2
  ScrubCount = 0
  SeamHidden = false
  SeamVisible = false
  SmoothHidden = false
  SmoothVisible = false
  Source = -> [Body001]
  Type = 4
  X = 0
  XDirection = (-1,0,2e-16)
  Y = -75.6668
FEATURE [TechDraw::DrawViewDimension] Dimension013
  AngleOverride = false
  Arbitrary = false
  ArbitraryTolerances = false
  EqualTolerance = false
  ExtensionAngle = 0
  FormatSpec = %.2f
  FormatSpecOverTolerance = %+.2w
  FormatSpecUnderTolerance = %+.2w
  Inverted = false
  LineAngle = 0
  LockPosition = false
  MeasureType = 1
  OverTolerance = 0
  References2D = -> [ProjItem001]
  Rotation = 0
  ScaleType = 0
  TheoreticalExact = false
  Type = 1
  UnderTolerance = -0.2
  X = 0.220775
  Y = 34.3046
FEATURE [TechDraw::DrawProjGroupItem] ProjItem002  label="Left"
  CoarseView = false
  Direction = (1,1e-16,-2e-16)
  Focus = 100
  HardHidden = false
  IsoCount = 0
  IsoHidden = false
  IsoVisible = false
  LockPosition = false
  Perspective = false
  Rotation = 0
  RotationVector = (-1e-16,1,0)
  ScaleType = 2
  ScrubCount = 0
  SeamHidden = false
  SeamVisible = false
  SmoothHidden = false
  SmoothVisible = false
  Source = -> [Body001]
  Type = 1
  X = 88.1389
  XDirection = (-1e-16,1,0)
  Y = 0
FEATURE [TechDraw::DrawProjGroup] ProjGroup
  Anchor = -> ProjItem
  AutoDistribute = false
  LockPosition = true
  ProjectionType = 1
  Rotation = 0
  ScaleType = 2
  Source = -> [Body001]
  Views = -> [ProjItem,ProjItem001,ProjItem002]
  X = 65.1601
  Y = 132.263
  spacingX = 50
  spacingY = 50
FEATURE [TechDraw::DrawViewPart] View
  CoarseView = false
  Direction = (-0.675,0.521,0.523)
  Focus = 100
  HardHidden = false
  IsoCount = 0
  IsoHidden = false
  IsoVisible = false
  LockPosition = true
  Perspective = false
  Rotation = 0
  ScaleType = 0
  ScrubCount = 0
  SeamHidden = false
  SeamVisible = false
  SmoothHidden = false
  SmoothVisible = false
  Source = -> [Body001]
  X = 245.336
  XDirection = (-0.611013,-0.79162,0)
  Y = 174.088
FEATURE [TechDraw::DrawViewAnnotation] Annotation  label="Notes"
  Font = DejaVu Sans
  LineSpace = 80
  LockPosition = true
  MaxWidth = -1
  Rotation = 0
  ScaleType = 0
  Text = Notes: | 1. Drill Hole \u23006.0 THRU | 2. Mating hole (H7) for part P/N: MISUMI GHCCG6-43, | Shaft Dia. D: 6, Tolerance: g6 (sliding fit) | 3. Material, PTFE | 4. This part is mating with part, P/N: Deployer - Rail
  TextSize = 4
  TextStyle = 0
  X = 65.3721
  Y = 185.184
FEATURE [TechDraw::DrawViewSection] DrawViewSection  label="Section A - A"
  BaseView = -> ProjItem001
  CoarseView = false
  CutSurfaceDisplay = 2
  Direction = (0,-1,0)
  FileGeomPattern = <path>
  Focus = 100
  FuseBeforeCut = true
  HardHidden = false
  HatchOffset = (0,0,0)
  HatchRotation = 0
  HatchScale = 1
  IsoCount = 0
  IsoHidden = false
  IsoVisible = false
  LockPosition = false
  NameGeomPattern = Diamond
  Perspective = false
  Rotation = 0
  ScaleType = 0
  ScrubCount = 0
  SeamHidden = false
  SeamVisible = false
  SectionDirection = 2
  SectionLineStretch = 1
  SectionNormal = (0,-1,0)
  SectionOrigin = (0,-25,17.5)
  SectionSymbol = A
  SmoothHidden = false
  SmoothVisible = false
  Source = -> [Body001]
  TrimAfterCut = false
  UsePreviousCut = false
  X = 239.047
  XDirection = (-1,0,2e-16)
  Y = 85.4975
FEATURE [TechDraw::DrawViewSymbol] Symbol
  LockPosition = false
  Rotation = 0
  ScaleType = 2
  Symbol = <blob: 3150 chars omitted>
  X = 259.119
  Y = 104.279
FEATURE [TechDraw::DrawSVGTemplate] Template
  EditableTexts = Designed_by_Name=Papamatthaiou M.; FC-Date=29/10/2019; FC-SC=1:1; FC-SHEET=1/1; FC-Title=PocketQube Pusher; MATERIAL=NOTE-3; REV=A; ROUGHNESS=-; Subtitle=pusher; TOLERANCES=DIN ISO 2768- mK; Weight=N/A
  Height = 210
  Orientation = 1
  Width = 297
FEATURE [TechDraw::DrawViewDimension] Dimension015
  AngleOverride = false
  Arbitrary = false
  ArbitraryTolerances = false
  EqualTolerance = false
  ExtensionAngle = 0
  FormatSpec = (Note-1) ⌀%.2f
  FormatSpecOverTolerance = %+.2w
  FormatSpecUnderTolerance = %+.2w
  Inverted = false
  LineAngle = 0
  LockPosition = false
  MeasureType = 1
  OverTolerance = 0
  References2D = -> [ProjItem001]
  Rotation = 0
  ScaleType = 0
  TheoreticalExact = false
  Type = 5
  UnderTolerance = 0
  X = 52.104
  Y = -9.97206
FEATURE [TechDraw::DrawViewDimension] Dimension016
  AngleOverride = false
  Arbitrary = false
  ArbitraryTolerances = false
  EqualTolerance = false
  ExtensionAngle = 0
  FormatSpec = %.2f
  FormatSpecOverTolerance = %+.2w
  FormatSpecUnderTolerance = %+.2w
  Inverted = false
  LineAngle = 0
  LockPosition = false
  MeasureType = 1
  OverTolerance = 0.1
  References2D = -> [ProjItem001]
  Rotation = 0
  ScaleType = 0
  TheoreticalExact = false
  Type = 1
  UnderTolerance = -0.1
  X = 48.8608
  Y = -29.8266
FEATURE [TechDraw::DrawViewDimension] Dimension017
  AngleOverride = false
  Arbitrary = false
  ArbitraryTolerances = false
  EqualTolerance = false
  ExtensionAngle = 0
  FormatSpec = %.2f
  FormatSpecOverTolerance = %+.2w
  FormatSpecUnderTolerance = %+.2w
  Inverted = false
  LineAngle = 0
  LockPosition = false
  MeasureType = 1
  OverTolerance = 0.1
  References2D = -> [ProjItem002]
  Rotation = 0
  ScaleType = 0
  TheoreticalExact = false
  Type = 2
  UnderTolerance = 0
  X = 35.9807
  Y = -22.5661
FEATURE [TechDraw::DrawViewDimension] Dimension018
  AngleOverride = false
  Arbitrary = false
  ArbitraryTolerances = false
  EqualTolerance = false
  ExtensionAngle = 0
  FormatSpec = %.2f
  FormatSpecOverTolerance = %+.2w
  FormatSpecUnderTolerance = %+.2w
  Inverted = false
  LineAngle = 0
  LockPosition = false
  MeasureType = 1
  OverTolerance = 0.1
  References2D = -> [ProjItem002]
  Rotation = 0
  ScaleType = 0
  TheoreticalExact = false
  Type = 1
  UnderTolerance = 0
  X = 13.9643
  Y = -27.3146
FEATURE [TechDraw::DrawViewDimension] Dimension019
  AngleOverride = false
  Arbitrary = false
  ArbitraryTolerances = false
  EqualTolerance = false
  ExtensionAngle = 0
  FormatSpec = (Note-2) ⌀%.2f
  FormatSpecOverTolerance = %+.2w
  FormatSpecUnderTolerance = %+.2w
  Inverted = false
  LineAngle = 0
  LockPosition = false
  MeasureType = 1
  OverTolerance = 0.01
  References2D = -> [ProjItem002]
  Rotation = 0
  ScaleType = 0
  TheoreticalExact = false
  Type = 5
  UnderTolerance = 0
  X = 26.4792
  Y = 20.6918
FEATURE [TechDraw::DrawPage] Page
  KeepUpdated = true
  NextBalloonIndex = 1
  ProjectionType = 0
  Template = -> Template
  Views = -> [ProjGroup,View,Dimension,Dimension001,Dimension002,Annotation,Dimension013,DrawViewSection,Symbol,Dimension015,Dimension016,Dimension017,Dimension018,Dimension019]
FEATURE [App::Part] Part  label="Pusher"
  Group = -> [Body001]
  Origin = -> Origin002
FEATURE [App::Part] Part001  label="Spool"
  Group = -> [Body]
  Origin = -> Origin003
note: 1 file-system path scrubbed to <path> (originals preserved in the JSON sidecar)
